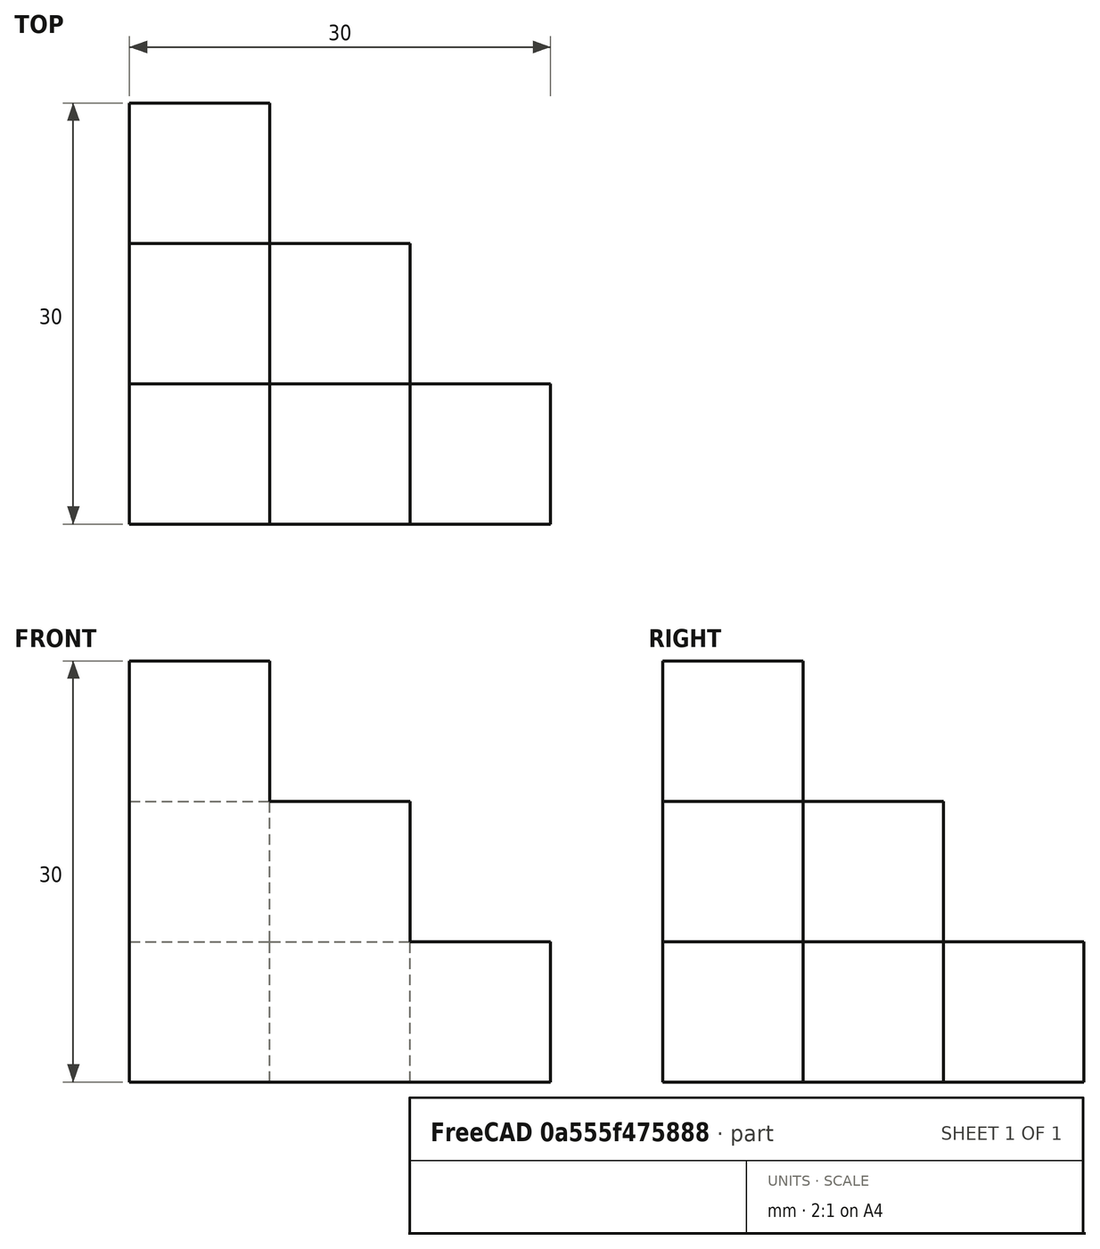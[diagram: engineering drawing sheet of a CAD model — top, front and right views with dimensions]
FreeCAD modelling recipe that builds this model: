
FCSTD DOCUMENT  (FreeCAD 1.0R39285 (Git))
Label: ojt1_t05r02_refineQbert_3-levels
License: All rights reserved
objects: Part::Box×6, Part::MultiFuse×1
note: 7 computed .brp shape members not serialized (recipe doc carries the construction recipe); baked Part::Feature solids carry a one-line shape summary decoded from their .brp

FEATURE [Part::Box] Box  label="Cub"
  AttacherType = Attacher::AttachEngine3D
  Height = 30
  Length = 10
  Width = 10
FEATURE [Part::Box] Box001  label="Cub001"
  AttacherType = Attacher::AttachEngine3D
  Height = 20
  Length = 10
  Placement = pos=(10,0,0) rot=(0,0,1;0rad)
  Width = 10
FEATURE [Part::Box] Box002  label="Cub002"
  AttacherType = Attacher::AttachEngine3D
  Height = 20
  Length = 10
  Placement = pos=(0,10,0) rot=(0,0,1;0rad)
  Width = 10
FEATURE [Part::Box] Box003  label="Cub003"
  AttacherType = Attacher::AttachEngine3D
  Height = 10
  Length = 10
  Placement = pos=(20,0,0) rot=(0,0,1;0rad)
  Width = 10
FEATURE [Part::Box] Box004  label="Cub004"
  AttacherType = Attacher::AttachEngine3D
  Height = 10
  Length = 10
  Placement = pos=(0,20,0) rot=(0,0,1;0rad)
  Width = 10
FEATURE [Part::Box] Box005  label="Cub005"
  AttacherType = Attacher::AttachEngine3D
  Height = 10
  Length = 10
  Placement = pos=(10,10,0) rot=(0,0,1;0rad)
  Width = 10
FEATURE [Part::MultiFuse] Fusion
  Refine = true
  Shapes = -> [Box,Box001,Box002,Box003,Box004,Box005]
